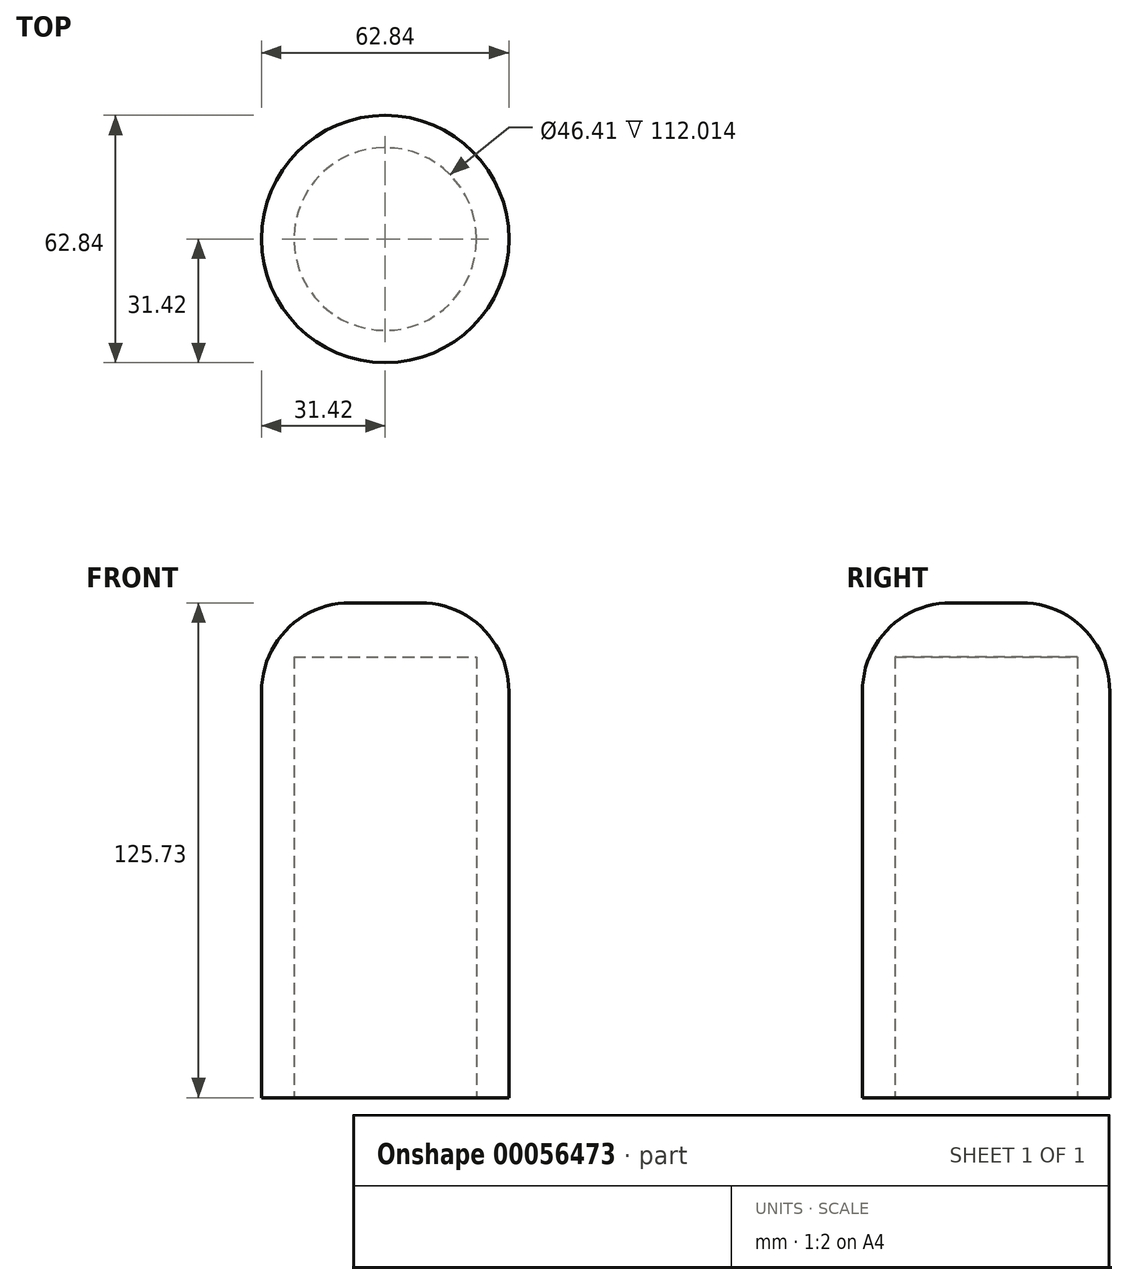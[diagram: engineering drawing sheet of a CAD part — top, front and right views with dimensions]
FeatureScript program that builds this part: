
annotation { "Feature Type Name" : "Feature", "Feature Type Description" : "" }
export const myFeature = defineFeature(function(context is Context, id is Id, definition is map)
    precondition{}
    {
        {
            var Q0;
            Q0=qCreatedBy(makeId("Top.planeOp"),FACE);
            var sketch = newSketch(context, id + "F0", { "sketchPlane" : qUnion([Q0])});
            skCircle(sketch, "E0", {"center": v(0, 0) * mm, "radius": 34.92 * mm});
            skSolve(sketch);
        }
        {
            var Q0;
            Q0=makeQuery(id+"F0.imprint","IMPRINT",FACE,{"disambiguationData":[TD([[makeQuery(id+"F0.imprint","IMPRINT",EDGE,{"derivedFrom":sQuery(id+"F0.wireOp",EDGE,"E0")}),1.0]])]});
            extrude(context, id + "F1", {"entities" : qUnion([Q0]), "depth" : 152.4 * mm});
        }
        {
            var Q0;
            Q0=makeQuery(id+"F1.opExtrude","CAP_EDGE",EDGE,{"disambiguationData":[OSD([sQuery(id+"F0.wireOp",EDGE,"E0")])],"isStart":false});
            fillet(context, id + "F2", {"entities" : qUnion([Q0]), "radius" : 25 * mm, "tangentPropagation" : true, "allowEdgeOverflow" : false});
        }
        {
            var Q0;
            Q0=makeQuery(id+"F1.opExtrude","CAP_FACE",FACE,{"disambiguationData":[OSD([sQuery(id+"F0.wireOp",EDGE,"E0")])],"isStart":true});
            var sketch = newSketch(context, id + "F3", { "sketchPlane" : qUnion([Q0])});
            skCircle(sketch, "E1", {"center": v(0, 0) * mm, "radius": 25.78 * mm});
            skSolve(sketch);
        }
        {
            var Q0;
            Q0=makeQuery(id+"F3.imprint","IMPRINT",FACE,{"disambiguationData":[TD([[makeQuery(id+"F3.imprint","IMPRINT",EDGE,{"derivedFrom":sQuery(id+"F3.wireOp",EDGE,"E1")}),1.0]])]});
            extrude(context, id + "F4", {"entities" : qUnion([Q0]), "operationType" : NewBodyOperationType.REMOVE, "oppositeDirection" : true, "depth" : 137.16 * mm});
        }
        {
            var Q0;
            Q0=makeQuery(id+"F1.opExtrude","CAP_FACE",FACE,{"disambiguationData":[OSD([sQuery(id+"F0.wireOp",EDGE,"E0")])],"isStart":true});
            extrude(context, id + "F5", {"entities" : qUnion([Q0]), "operationType" : NewBodyOperationType.REMOVE, "oppositeDirection" : true, "depth" : 12.7 * mm});
        }
        {
            var Q0;
            Q0=makeQuery(id+"F1.opExtrude","SWEPT_BODY",BODY,{"disambiguationData":[OSD([sQuery(id+"F0.wireOp",EDGE,"E0")])]});
            var Q1;
            Q1=qCreatedBy(makeId("Origin.pointOp"),VERTEX);
            transform(context, id + "F6", {"entities" : qUnion([Q0]), "transformType" : TransformType.SCALE_UNIFORMLY, "scale" : .9, "scalePoint" : qUnion([Q1]), "makeCopy" : false});
        }
    });
